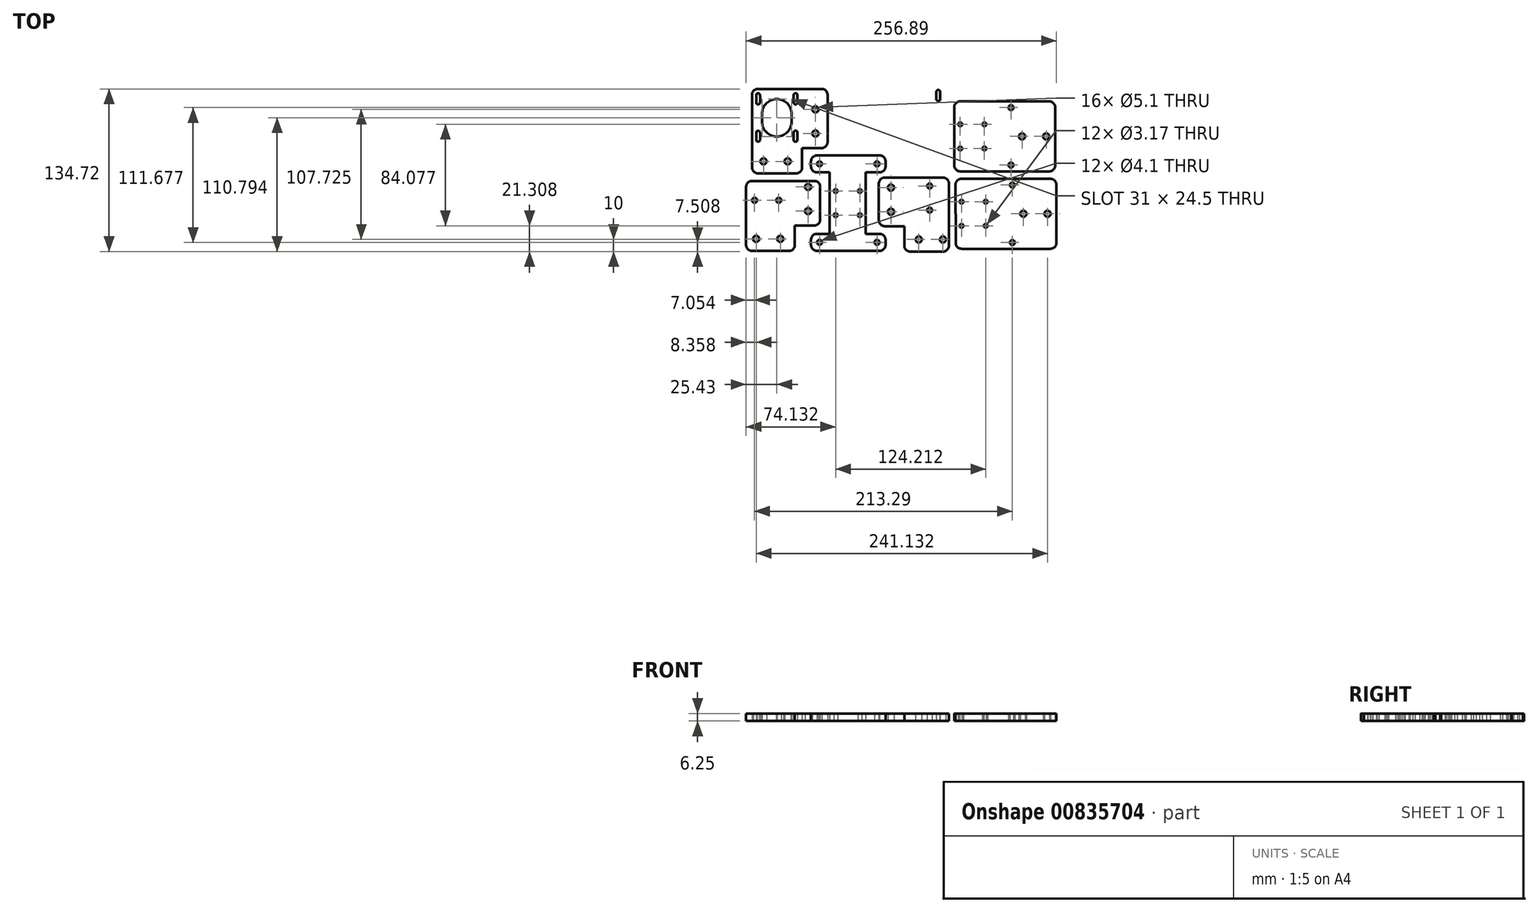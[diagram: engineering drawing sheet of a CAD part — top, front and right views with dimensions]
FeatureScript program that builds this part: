
annotation { "Feature Type Name" : "Feature", "Feature Type Description" : "" }
export const myFeature = defineFeature(function(context is Context, id is Id, definition is map)
    precondition{}
    {
        {
            var Q0;
            Q0=qCreatedBy(makeId("Top.planeOp"),FACE);
            var sketch = newSketch(context, id + "F0", { "sketchPlane" : qUnion([Q0])});
            skCircle(sketch, "E0", {"center": v(84.47, -229.67) * mm, "radius": 2.05 * mm});
            skCircle(sketch, "E1", {"center": v(84.47, -209.67) * mm, "radius": 2.05 * mm});
            skCircle(sketch, "E2", {"center": v(52.47, -210.97) * mm, "radius": 2.55 * mm});
            skCircle(sketch, "E3", {"center": v(52.47, -230.97) * mm, "radius": 2.55 * mm});
            skCircle(sketch, "E4", {"center": v(75.47, -253.97) * mm, "radius": 2.55 * mm});
            skCircle(sketch, "E5", {"center": v(95.47, -253.97) * mm, "radius": 2.55 * mm});
            skLineSegment(sketch, "E6.top", {"start": v(68.47, -263.97) * mm, "end": v(95.47, -263.97) * mm});
            skLineSegment(sketch, "E6.left", {"start": v(42.47, -207.62) * mm, "end": v(42.47, -237.97) * mm});
            skLineSegment(sketch, "E7.top", {"start": v(47.47, -242.97) * mm, "end": v(63.47, -242.97) * mm});
            skLineSegment(sketch, "E7.right", {"start": v(63.47, -258.97) * mm, "end": v(63.47, -242.97) * mm});
            skLineSegment(sketch, "E8", {"start": v(100.47, -258.97) * mm, "end": v(100.47, -207.62) * mm});
            skLineSegment(sketch, "E9", {"start": v(47.47, -202.62) * mm, "end": v(95.47, -202.62) * mm});
            skArc(sketch, "E10.filletArc", {"start": v(95.47, -263.97) * mm, "mid": v(99, -262.5) * mm, "end": v(100.47, -258.97) * mm});
            skArc(sketch, "E11.filletArc", {"start": v(47.47, -202.62) * mm, "mid": v(43.94, -204.08) * mm, "end": v(42.47, -207.62) * mm});
            skArc(sketch, "E12.filletArc", {"start": v(100.47, -207.62) * mm, "mid": v(99, -204.08) * mm, "end": v(95.47, -202.62) * mm});
            skArc(sketch, "E13.filletArc", {"start": v(63.47, -258.97) * mm, "mid": v(64.94, -262.5) * mm, "end": v(68.47, -263.97) * mm});
            skArc(sketch, "E14.filletArc", {"start": v(42.47, -237.97) * mm, "mid": v(43.94, -241.5) * mm, "end": v(47.47, -242.97) * mm});
            skCircle(sketch, "E15", {"center": v(-6.65, -191.33) * mm, "radius": 2.05 * mm});
            skCircle(sketch, "E16", {"center": v(40.95, -191.33) * mm, "radius": 2.05 * mm});
            skCircle(sketch, "E17", {"center": v(6.7, -233.83) * mm, "radius": 1.59 * mm});
            skCircle(sketch, "E18", {"center": v(6.7, -213.83) * mm, "radius": 1.59 * mm});
            skCircle(sketch, "E19", {"center": v(26.7, -233.83) * mm, "radius": 1.59 * mm});
            skCircle(sketch, "E20", {"center": v(26.7, -213.83) * mm, "radius": 1.59 * mm});
            skCircle(sketch, "E21", {"center": v(-6.65, -256.33) * mm, "radius": 2.05 * mm});
            skCircle(sketch, "E22", {"center": v(40.95, -256.33) * mm, "radius": 2.05 * mm});
            skLineSegment(sketch, "E23.top", {"start": v(1.7, -249.28) * mm, "end": v(1.7, -198.38) * mm});
            skLineSegment(sketch, "E23.left", {"start": v(-8.7, -249.28) * mm, "end": v(1.7, -249.28) * mm});
            skLineSegment(sketch, "E24.bottom", {"start": v(-13.7, -258.38) * mm, "end": v(-13.7, -254.28) * mm});
            skLineSegment(sketch, "E24.top", {"start": v(48, -193.38) * mm, "end": v(48, -189.28) * mm});
            skLineSegment(sketch, "E24.left", {"start": v(-8.7, -263.38) * mm, "end": v(43, -263.38) * mm});
            skLineSegment(sketch, "E24.right", {"start": v(-8.7, -184.28) * mm, "end": v(43, -184.28) * mm});
            skLineSegment(sketch, "E25.top", {"start": v(31.7, -249.28) * mm, "end": v(31.7, -198.38) * mm});
            skLineSegment(sketch, "E25.left", {"start": v(43, -249.28) * mm, "end": v(31.7, -249.28) * mm});
            skLineSegment(sketch, "E25.right", {"start": v(43, -198.38) * mm, "end": v(31.7, -198.38) * mm});
            skArc(sketch, "E26.filletArc", {"start": v(-8.7, -249.28) * mm, "mid": v(-12.24, -250.75) * mm, "end": v(-13.7, -254.28) * mm});
            skArc(sketch, "E27.filletArc", {"start": v(-13.7, -258.38) * mm, "mid": v(-12.24, -261.92) * mm, "end": v(-8.7, -263.38) * mm});
            skLineSegment(sketch, "E28", {"start": v(-13.7, -193.38) * mm, "end": v(-13.7, -189.28) * mm});
            skLineSegment(sketch, "E29", {"start": v(1.7, -198.38) * mm, "end": v(-8.7, -198.38) * mm});
            skArc(sketch, "E30.filletArc", {"start": v(-13.7, -193.38) * mm, "mid": v(-12.24, -196.92) * mm, "end": v(-8.7, -198.38) * mm});
            skArc(sketch, "E31.filletArc", {"start": v(-8.7, -184.28) * mm, "mid": v(-12.24, -185.75) * mm, "end": v(-13.7, -189.28) * mm});
            skArc(sketch, "E32.filletArc", {"start": v(48, -189.28) * mm, "mid": v(46.54, -185.75) * mm, "end": v(43, -184.28) * mm});
            skArc(sketch, "E33.filletArc", {"start": v(43, -198.38) * mm, "mid": v(46.54, -196.92) * mm, "end": v(48, -193.38) * mm});
            skLineSegment(sketch, "E34", {"start": v(48, -258.38) * mm, "end": v(48, -254.28) * mm});
            skArc(sketch, "E35.filletArc", {"start": v(48, -254.28) * mm, "mid": v(46.54, -250.75) * mm, "end": v(43, -249.28) * mm});
            skArc(sketch, "E36.filletArc", {"start": v(43, -263.38) * mm, "mid": v(46.54, -261.92) * mm, "end": v(48, -258.38) * mm});
            skCircle(sketch, "E37", {"center": v(-40.38, -221.45) * mm, "radius": 2.05 * mm});
            skCircle(sketch, "E38", {"center": v(-60.38, -221.45) * mm, "radius": 2.05 * mm});
            skCircle(sketch, "E39", {"center": v(-59.07, -253.45) * mm, "radius": 2.55 * mm});
            skCircle(sketch, "E40", {"center": v(-39.07, -253.45) * mm, "radius": 2.55 * mm});
            skCircle(sketch, "E41", {"center": v(-16.07, -230.45) * mm, "radius": 2.55 * mm});
            skCircle(sketch, "E42", {"center": v(-16.07, -210.45) * mm, "radius": 2.55 * mm});
            skLineSegment(sketch, "E43.top", {"start": v(-6.07, -237.45) * mm, "end": v(-6.07, -210.45) * mm});
            skLineSegment(sketch, "E43.left", {"start": v(-62.43, -263.45) * mm, "end": v(-32.07, -263.45) * mm});
            skLineSegment(sketch, "E44.top", {"start": v(-27.07, -258.45) * mm, "end": v(-27.07, -242.45) * mm});
            skLineSegment(sketch, "E44.right", {"start": v(-11.07, -242.45) * mm, "end": v(-27.07, -242.45) * mm});
            skLineSegment(sketch, "E45", {"start": v(-11.07, -205.45) * mm, "end": v(-62.43, -205.45) * mm});
            skLineSegment(sketch, "E46", {"start": v(-67.43, -258.45) * mm, "end": v(-67.43, -210.45) * mm});
            skArc(sketch, "E47.filletArc", {"start": v(-6.07, -210.45) * mm, "mid": v(-7.54, -206.92) * mm, "end": v(-11.07, -205.45) * mm});
            skArc(sketch, "E48.filletArc", {"start": v(-67.43, -258.45) * mm, "mid": v(-65.96, -261.99) * mm, "end": v(-62.43, -263.45) * mm});
            skArc(sketch, "E49.filletArc", {"start": v(-62.43, -205.45) * mm, "mid": v(-65.96, -206.92) * mm, "end": v(-67.43, -210.45) * mm});
            skArc(sketch, "E50.filletArc", {"start": v(-11.07, -242.45) * mm, "mid": v(-7.54, -240.99) * mm, "end": v(-6.07, -237.45) * mm});
            skArc(sketch, "E51.filletArc", {"start": v(-32.07, -263.45) * mm, "mid": v(-28.54, -261.99) * mm, "end": v(-27.07, -258.45) * mm});
            skLineSegment(sketch, "E52.bottom", {"start": v(-68.68, -266.48) * mm, "end": v(191.32, -266.48) * mm});
            skLineSegment(sketch, "E52.top", {"start": v(-68.68, -126.48) * mm, "end": v(191.32, -126.48) * mm});
            skLineSegment(sketch, "E52.left", {"start": v(-68.68, -266.48) * mm, "end": v(-68.68, -126.48) * mm});
            skLineSegment(sketch, "E52.right", {"start": v(191.32, -266.48) * mm, "end": v(191.32, -126.48) * mm});
            skCircle(sketch, "E53", {"center": v(152.91, -208.86) * mm, "radius": 2.05 * mm});
            skCircle(sketch, "E54", {"center": v(152.91, -256.46) * mm, "radius": 2.05 * mm});
            skCircle(sketch, "E55", {"center": v(162.06, -232.66) * mm, "radius": 2.55 * mm});
            skCircle(sketch, "E56", {"center": v(182.06, -232.66) * mm, "radius": 2.55 * mm});
            skCircle(sketch, "E57", {"center": v(110.91, -222.66) * mm, "radius": 1.59 * mm});
            skCircle(sketch, "E58", {"center": v(130.91, -222.66) * mm, "radius": 1.59 * mm});
            skCircle(sketch, "E59", {"center": v(110.91, -242.66) * mm, "radius": 1.59 * mm});
            skCircle(sketch, "E60", {"center": v(130.91, -242.66) * mm, "radius": 1.59 * mm});
            skLineSegment(sketch, "E61.right", {"start": v(189.46, -208.66) * mm, "end": v(189.46, -256.66) * mm});
            skLineSegment(sketch, "E62", {"start": v(105.87, -208.68) * mm, "end": v(106.03, -256.68) * mm});
            skLineSegment(sketch, "E63", {"start": v(110.87, -203.66) * mm, "end": v(184.46, -203.66) * mm});
            skLineSegment(sketch, "E64", {"start": v(184.46, -261.66) * mm, "end": v(111.03, -261.66) * mm});
            skArc(sketch, "E65.filletArc", {"start": v(110.87, -203.66) * mm, "mid": v(107.33, -205.13) * mm, "end": v(105.87, -208.68) * mm});
            skArc(sketch, "E66.filletArc", {"start": v(189.46, -208.66) * mm, "mid": v(188, -205.13) * mm, "end": v(184.46, -203.66) * mm});
            skArc(sketch, "E67.filletArc", {"start": v(184.46, -261.66) * mm, "mid": v(188, -260.2) * mm, "end": v(189.46, -256.66) * mm});
            skArc(sketch, "E68.filletArc", {"start": v(106.03, -256.68) * mm, "mid": v(107.5, -260.2) * mm, "end": v(111.03, -261.66) * mm});
            skCircle(sketch, "E69", {"center": v(151.8, -144.79) * mm, "radius": 2.05 * mm});
            skCircle(sketch, "E70", {"center": v(151.8, -192.39) * mm, "radius": 2.05 * mm});
            skCircle(sketch, "E71", {"center": v(160.95, -168.59) * mm, "radius": 2.55 * mm});
            skCircle(sketch, "E72", {"center": v(180.95, -168.59) * mm, "radius": 2.55 * mm});
            skCircle(sketch, "E73", {"center": v(109.8, -158.59) * mm, "radius": 1.59 * mm});
            skCircle(sketch, "E74", {"center": v(129.8, -158.59) * mm, "radius": 1.59 * mm});
            skCircle(sketch, "E75", {"center": v(109.8, -178.59) * mm, "radius": 1.59 * mm});
            skCircle(sketch, "E76", {"center": v(129.8, -178.59) * mm, "radius": 1.59 * mm});
            skLineSegment(sketch, "E77.right", {"start": v(188.35, -144.59) * mm, "end": v(188.35, -192.59) * mm});
            skLineSegment(sketch, "E78", {"start": v(104.76, -144.6) * mm, "end": v(104.92, -192.6) * mm});
            skLineSegment(sketch, "E79", {"start": v(109.76, -139.59) * mm, "end": v(183.35, -139.59) * mm});
            skLineSegment(sketch, "E80", {"start": v(183.35, -197.59) * mm, "end": v(109.92, -197.59) * mm});
            skArc(sketch, "E81.filletArc", {"start": v(109.76, -139.59) * mm, "mid": v(106.22, -141.06) * mm, "end": v(104.76, -144.6) * mm});
            skArc(sketch, "E82.filletArc", {"start": v(188.35, -144.59) * mm, "mid": v(186.89, -141.05) * mm, "end": v(183.35, -139.59) * mm});
            skArc(sketch, "E83.filletArc", {"start": v(183.35, -197.59) * mm, "mid": v(186.89, -196.12) * mm, "end": v(188.35, -192.59) * mm});
            skArc(sketch, "E84.filletArc", {"start": v(104.92, -192.6) * mm, "mid": v(106.39, -196.13) * mm, "end": v(109.92, -197.59) * mm});
            skCircle(sketch, "E85", {"center": v(-53, -189.25) * mm, "radius": 2.55 * mm});
            skCircle(sketch, "E86", {"center": v(-33, -189.25) * mm, "radius": 2.55 * mm});
            skCircle(sketch, "E87", {"center": v(-10, -166.25) * mm, "radius": 2.55 * mm});
            skCircle(sketch, "E88", {"center": v(-10, -146.25) * mm, "radius": 2.55 * mm});
            skLineSegment(sketch, "E89.top", {"start": v(0, -173.25) * mm, "end": v(0, -134.25) * mm});
            skLineSegment(sketch, "E89.left", {"start": v(-57.5, -199.25) * mm, "end": v(-26, -199.25) * mm});
            skLineSegment(sketch, "E89.right", {"start": v(-57.5, -129.25) * mm, "end": v(-5, -129.25) * mm});
            skLineSegment(sketch, "E90.top", {"start": v(-21, -194.25) * mm, "end": v(-21, -178.25) * mm});
            skLineSegment(sketch, "E90.right", {"start": v(-5, -178.25) * mm, "end": v(-21, -178.25) * mm});
            skLineSegment(sketch, "E91", {"start": v(-62.5, -134.25) * mm, "end": v(-62.5, -194.25) * mm});
            skLineSegment(sketch, "E92", {"start": v(-57.5, -165.43) * mm, "end": v(-57.5, -171.43) * mm});
            skLineSegment(sketch, "E93", {"start": v(-26.5, -165.43) * mm, "end": v(-26.5, -171.43) * mm});
            skLineSegment(sketch, "E94", {"start": v(-57.5, -134.43) * mm, "end": v(-57.5, -140.43) * mm});
            skLineSegment(sketch, "E95", {"start": v(-54.25, -156.43) * mm, "end": v(-54.25, -149.93) * mm});
            skLineSegment(sketch, "E96", {"start": v(-29.75, -156.43) * mm, "end": v(-29.75, -149.93) * mm});
            skArc(sketch, "E97", {"start": v(-54.25, -156.43) * mm, "mid": v(-42, -168.68) * mm, "end": v(-29.75, -156.43) * mm});
            skArc(sketch, "E98", {"start": v(-29.75, -149.93) * mm, "mid": v(-42, -137.68) * mm, "end": v(-54.25, -149.93) * mm});
            skLineSegment(sketch, "E99", {"start": v(-55.91, -140.48) * mm, "end": v(-55.91, -134.47) * mm});
            skLineSegment(sketch, "E100", {"start": v(-59.09, -140.48) * mm, "end": v(-59.09, -134.47) * mm});
            skLineSegment(sketch, "E101", {"start": v(-28.09, -140.51) * mm, "end": v(-28.09, -134.47) * mm});
            skLineSegment(sketch, "E102", {"start": v(-24.91, -140.48) * mm, "end": v(-24.91, -134.43) * mm});
            skLineSegment(sketch, "E103", {"start": v(-26.5, -140.43) * mm, "end": v(-26.5, -134.43) * mm});
            skLineSegment(sketch, "E104", {"start": v(-24.91, -171.43) * mm, "end": v(-24.91, -165.41) * mm});
            skLineSegment(sketch, "E105", {"start": v(-28.09, -171.43) * mm, "end": v(-28.09, -165.41) * mm});
            skLineSegment(sketch, "E106", {"start": v(-55.91, -171.44) * mm, "end": v(-55.91, -165.44) * mm});
            skLineSegment(sketch, "E107", {"start": v(-59.09, -171.44) * mm, "end": v(-59.09, -165.44) * mm});
            skArc(sketch, "E108", {"start": v(-59.09, -171.44) * mm, "mid": v(-57.5, -173.02) * mm, "end": v(-55.91, -171.44) * mm});
            skArc(sketch, "E109", {"start": v(-55.91, -165.44) * mm, "mid": v(-57.5, -163.85) * mm, "end": v(-59.09, -165.44) * mm});
            skArc(sketch, "E110", {"start": v(-28.09, -171.43) * mm, "mid": v(-26.5, -173.02) * mm, "end": v(-24.91, -171.43) * mm});
            skArc(sketch, "E111", {"start": v(-24.91, -165.41) * mm, "mid": v(-26.5, -163.83) * mm, "end": v(-28.09, -165.41) * mm});
            skArc(sketch, "E112", {"start": v(-28.09, -140.51) * mm, "mid": v(-26.48, -142.06) * mm, "end": v(-24.91, -140.48) * mm});
            skArc(sketch, "E113", {"start": v(-24.91, -134.43) * mm, "mid": v(-26.52, -132.85) * mm, "end": v(-28.09, -134.47) * mm});
            skArc(sketch, "E114", {"start": v(-55.91, -134.47) * mm, "mid": v(-57.5, -132.88) * mm, "end": v(-59.09, -134.47) * mm});
            skArc(sketch, "E115", {"start": v(-59.09, -140.48) * mm, "mid": v(-57.5, -142.06) * mm, "end": v(-55.91, -140.48) * mm});
            skArc(sketch, "E116.filletArc", {"start": v(-26, -199.25) * mm, "mid": v(-22.46, -197.78) * mm, "end": v(-21, -194.25) * mm});
            skArc(sketch, "E117.filletArc", {"start": v(-62.5, -194.25) * mm, "mid": v(-61.04, -197.78) * mm, "end": v(-57.5, -199.25) * mm});
            skArc(sketch, "E118.filletArc", {"start": v(-5, -178.25) * mm, "mid": v(-1.46, -176.78) * mm, "end": v(0, -173.25) * mm});
            skArc(sketch, "E119.filletArc", {"start": v(0, -134.25) * mm, "mid": v(-1.46, -130.71) * mm, "end": v(-5, -129.25) * mm});
            skArc(sketch, "E120.filletArc", {"start": v(-57.5, -129.25) * mm, "mid": v(-61.04, -130.71) * mm, "end": v(-62.5, -134.25) * mm});
            skArc(sketch, "E121.MirrorCS", {"start": v(90.04, -131.7) * mm, "mid": v(91.62, -130.11) * mm, "end": v(93.21, -131.7) * mm});
            skLineSegment(sketch, "E122.MirrorCS", {"start": v(90.04, -137.7) * mm, "end": v(90.04, -131.7) * mm});
            skLineSegment(sketch, "E123.MirrorCS", {"start": v(90.04, -168.67) * mm, "end": v(90.04, -162.67) * mm});
            skArc(sketch, "E124.MirrorCS", {"start": v(59.04, -162.65) * mm, "mid": v(60.62, -161.06) * mm, "end": v(62.21, -162.65) * mm});
            skArc(sketch, "E125.MirrorCS", {"start": v(90.04, -162.67) * mm, "mid": v(91.62, -161.08) * mm, "end": v(93.21, -162.67) * mm});
            skArc(sketch, "E126.MirrorCS", {"start": v(93.21, -168.67) * mm, "mid": v(91.62, -170.26) * mm, "end": v(90.04, -168.67) * mm});
            skLineSegment(sketch, "E127.MirrorCS", {"start": v(93.21, -137.7) * mm, "end": v(93.21, -131.7) * mm});
            skLineSegment(sketch, "E128.MirrorCS", {"start": v(93.21, -168.67) * mm, "end": v(93.21, -162.67) * mm});
            skLineSegment(sketch, "E129.MirrorCS", {"start": v(91.62, -162.66) * mm, "end": v(91.62, -168.66) * mm});
            skArc(sketch, "E130.MirrorCS", {"start": v(93.21, -137.7) * mm, "mid": v(91.62, -139.3) * mm, "end": v(90.04, -137.7) * mm});
            skLineSegment(sketch, "E131.MirrorCS", {"start": v(91.62, -131.66) * mm, "end": v(91.62, -137.66) * mm});
            skLineSegment(sketch, "E132.MirrorCS", {"start": v(60.62, -137.66) * mm, "end": v(60.62, -131.66) * mm});
            skArc(sketch, "E133.MirrorCS", {"start": v(34.12, -131.48) * mm, "mid": v(35.59, -127.94) * mm, "end": v(39.12, -126.48) * mm});
            skArc(sketch, "E134.MirrorCS", {"start": v(62.2, -137.74) * mm, "mid": v(60.6, -139.3) * mm, "end": v(59.04, -137.7) * mm});
            skArc(sketch, "E135.MirrorCS", {"start": v(62.21, -168.66) * mm, "mid": v(60.62, -170.25) * mm, "end": v(59.04, -168.66) * mm});
            skLineSegment(sketch, "E136.MirrorCS", {"start": v(63.87, -153.66) * mm, "end": v(63.87, -147.16) * mm});
            skLineSegment(sketch, "E137.MirrorCS", {"start": v(88.37, -153.66) * mm, "end": v(88.37, -147.16) * mm});
            skLineSegment(sketch, "E138.MirrorCS", {"start": v(59.04, -137.7) * mm, "end": v(59.04, -131.67) * mm});
            skArc(sketch, "E139.MirrorCS", {"start": v(39.12, -175.48) * mm, "mid": v(35.59, -174.01) * mm, "end": v(34.12, -170.48) * mm});
            skLineSegment(sketch, "E140.MirrorCS", {"start": v(62.21, -168.66) * mm, "end": v(62.21, -162.65) * mm});
            skLineSegment(sketch, "E141.MirrorCS", {"start": v(62.2, -137.74) * mm, "end": v(62.21, -131.7) * mm});
            skArc(sketch, "E142.MirrorCS", {"start": v(96.62, -191.48) * mm, "mid": v(95.16, -195.01) * mm, "end": v(91.62, -196.48) * mm});
            skArc(sketch, "E143.MirrorCS", {"start": v(60.12, -196.48) * mm, "mid": v(56.59, -195.01) * mm, "end": v(55.12, -191.48) * mm});
            skArc(sketch, "E144.MirrorCS", {"start": v(59.04, -131.67) * mm, "mid": v(60.64, -130.08) * mm, "end": v(62.21, -131.7) * mm});
            skLineSegment(sketch, "E145.MirrorCS", {"start": v(60.62, -162.66) * mm, "end": v(60.62, -168.66) * mm});
            skArc(sketch, "E146.MirrorCS", {"start": v(91.62, -126.48) * mm, "mid": v(95.16, -127.94) * mm, "end": v(96.62, -131.48) * mm});
            skLineSegment(sketch, "E147.MirrorCS", {"start": v(59.04, -168.66) * mm, "end": v(59.04, -162.65) * mm});
            skCircle(sketch, "E148.MirrorC", {"center": v(44.12, -143.48) * mm, "radius": 2.55 * mm});
            skCircle(sketch, "E149.MirrorC", {"center": v(44.12, -163.48) * mm, "radius": 2.55 * mm});
            skCircle(sketch, "E150.MirrorC", {"center": v(67.12, -186.48) * mm, "radius": 2.55 * mm});
            skCircle(sketch, "E151.MirrorC", {"center": v(87.12, -186.48) * mm, "radius": 2.55 * mm});
            skLineSegment(sketch, "E152.MirrorCS", {"start": v(96.62, -131.48) * mm, "end": v(96.62, -191.48) * mm});
            skLineSegment(sketch, "E153.MirrorCS", {"start": v(39.12, -175.48) * mm, "end": v(55.12, -175.48) * mm});
            skLineSegment(sketch, "E154.MirrorCS", {"start": v(91.62, -126.48) * mm, "end": v(39.12, -126.48) * mm});
            skLineSegment(sketch, "E155.MirrorCS", {"start": v(55.12, -191.48) * mm, "end": v(55.12, -175.48) * mm});
            skLineSegment(sketch, "E156.MirrorCS", {"start": v(91.62, -196.48) * mm, "end": v(60.12, -196.48) * mm});
            skLineSegment(sketch, "E157.MirrorCS", {"start": v(34.12, -170.48) * mm, "end": v(34.12, -131.48) * mm});
            skArc(sketch, "E158.MirrorCS", {"start": v(88.37, -153.66) * mm, "mid": v(76.12, -165.9) * mm, "end": v(63.87, -153.66) * mm});
            skArc(sketch, "E159.MirrorCS", {"start": v(63.87, -147.16) * mm, "mid": v(76.12, -134.9) * mm, "end": v(88.37, -147.16) * mm});
            skSolve(sketch);
        }
        {
            var Q0;
            Q0=makeQuery(id+"F0.imprint","IMPRINT",FACE,{"disambiguationData":[TD([[makeQuery(id+"F0.imprint","IMPRINT",EDGE,{"derivedFrom":sQuery(id+"F0.wireOp",EDGE,"E37")}),-1.0]])]});
            var Q1;
            Q1=makeQuery(id+"F0.imprint","IMPRINT",FACE,{"disambiguationData":[TD([[makeQuery(id+"F0.imprint","IMPRINT",EDGE,{"derivedFrom":sQuery(id+"F0.wireOp",EDGE,"E15")}),-1.0]])]});
            var Q2;
            Q2=makeQuery(id+"F0.imprint","IMPRINT",FACE,{"disambiguationData":[TD([[makeQuery(id+"F0.imprint","IMPRINT",EDGE,{"derivedFrom":sQuery(id+"F0.wireOp",EDGE,"E85")}),-1.0]])]});
            var Q3;
            Q3=makeQuery(id+"F0.imprint","IMPRINT",FACE,{"disambiguationData":[TD([[makeQuery(id+"F0.imprint","IMPRINT",EDGE,{"derivedFrom":sQuery(id+"F0.wireOp",EDGE,"E0")}),-1.0]])]});
            var Q4;
            Q4=makeQuery(id+"F0.imprint","IMPRINT",FACE,{"disambiguationData":[TD([[makeQuery(id+"F0.imprint","IMPRINT",EDGE,{"derivedFrom":sQuery(id+"F0.wireOp",EDGE,"E121.MirrorCS")}),1.0]])]});
            var Q5;
            Q5=makeQuery(id+"F0.imprint","IMPRINT",FACE,{"disambiguationData":[TD([[makeQuery(id+"F0.imprint","IMPRINT",EDGE,{"derivedFrom":sQuery(id+"F0.wireOp",EDGE,"E53")}),-1.0]])]});
            var Q6;
            Q6=makeQuery(id+"F0.imprint","IMPRINT",FACE,{"disambiguationData":[TD([[makeQuery(id+"F0.imprint","IMPRINT",EDGE,{"derivedFrom":sQuery(id+"F0.wireOp",EDGE,"E69")}),-1.0]])]});
            extrude(context, id + "F1", {"entities" : qUnion([Q0, Q1, Q2, Q3, Q4, Q5, Q6]), "depth" : 6.25 * mm, "offsetDistance" : 25 * mm});
        }
    });
